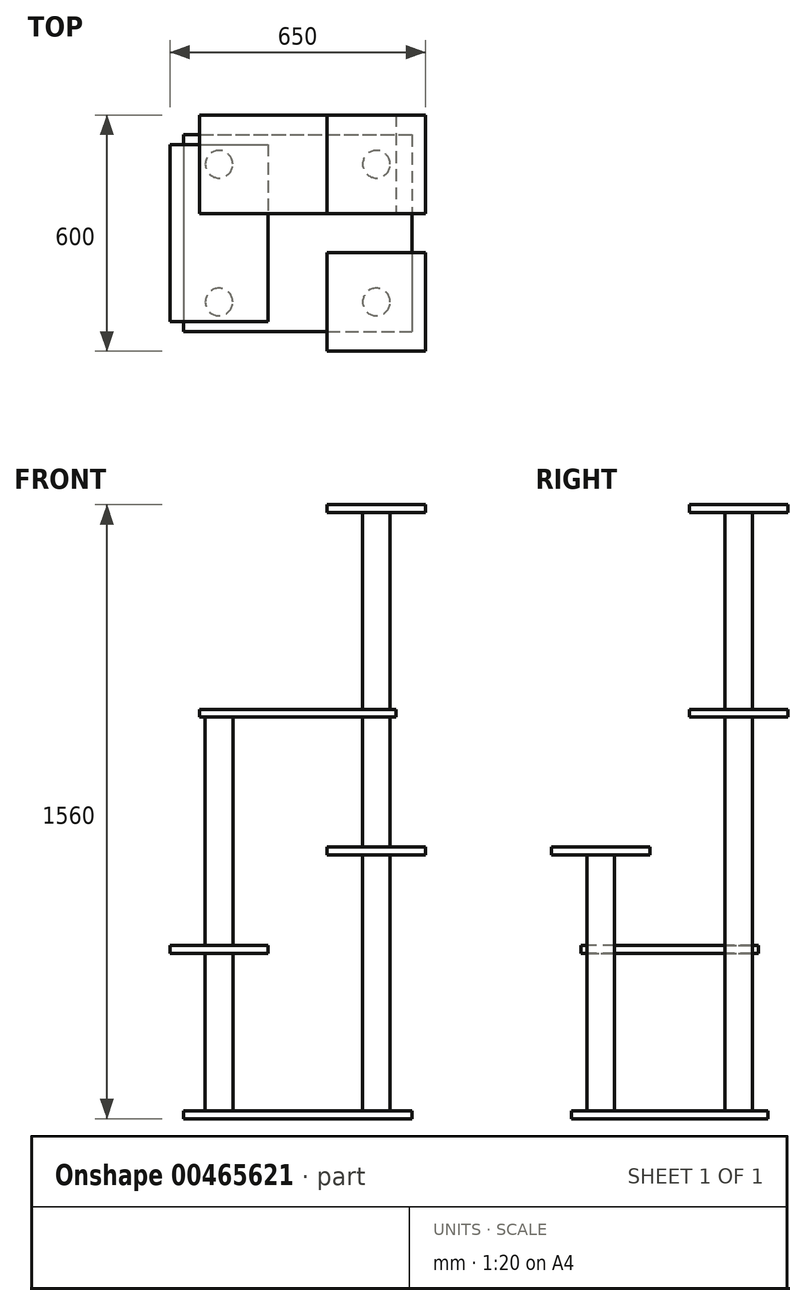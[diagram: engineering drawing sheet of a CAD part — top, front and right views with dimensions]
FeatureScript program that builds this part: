
annotation { "Feature Type Name" : "Feature", "Feature Type Description" : "" }
export const myFeature = defineFeature(function(context is Context, id is Id, definition is map)
    precondition{}
    {
        {
            var Q0;
            Q0=qCreatedBy(makeId("Top.planeOp"),FACE);
            var sketch = newSketch(context, id + "F0", { "sketchPlane" : qUnion([Q0])});
            skLineSegment(sketch, "E0.bottom", {"start": v(-290, 250) * mm, "end": v(290, 250) * mm});
            skLineSegment(sketch, "E0.top", {"start": v(-290, -250) * mm, "end": v(290, -250) * mm});
            skLineSegment(sketch, "E0.left", {"start": v(-290, 250) * mm, "end": v(-290, -250) * mm});
            skLineSegment(sketch, "E0.right", {"start": v(290, 250) * mm, "end": v(290, -250) * mm});
            skPoint(sketch, "E0.middle", {"position": v(0, 0) * mm});
            skSolve(sketch);
        }
        {
            var Q0;
            Q0=qSketchRegion(id+"F0",true);
            extrude(context, id + "F1", {"entities" : qUnion([Q0]), "depth" : 20 * mm});
        }
        {
            var Q0;
            Q0=makeQuery(id+"F1.opExtrude","CAP_FACE",FACE,{"disambiguationData":[OSD([sQuery(id+"F0.wireOp",EDGE,"E0.bottom"),sQuery(id+"F0.wireOp",EDGE,"E0.top"),sQuery(id+"F0.wireOp",EDGE,"E0.left"),sQuery(id+"F0.wireOp",EDGE,"E0.right")])],"isStart":false});
            var sketch = newSketch(context, id + "F2", { "sketchPlane" : qUnion([Q0])});
            skLineSegment(sketch, "E1.bottom", {"start": v(-200, 175) * mm, "end": v(200, 175) * mm, "construction": true});
            skLineSegment(sketch, "E1.top", {"start": v(-200, -175) * mm, "end": v(200, -175) * mm, "construction": true});
            skLineSegment(sketch, "E1.left", {"start": v(-200, 175) * mm, "end": v(-200, -175) * mm, "construction": true});
            skLineSegment(sketch, "E1.right", {"start": v(200, 175) * mm, "end": v(200, -175) * mm, "construction": true});
            skPoint(sketch, "E1.middle", {"position": v(0, 0) * mm});
            skCircle(sketch, "E2", {"center": v(-200, 175) * mm, "radius": 35 * mm});
            skCircle(sketch, "E3", {"center": v(200, 175) * mm, "radius": 35 * mm});
            skCircle(sketch, "E4", {"center": v(-200, -175) * mm, "radius": 35 * mm});
            skCircle(sketch, "E5", {"center": v(200, -175) * mm, "radius": 35 * mm});
            skSolve(sketch);
        }
        {
            var Q0;
            Q0=makeQuery(id+"F2.imprint","IMPRINT",FACE,{"disambiguationData":[TD([[makeQuery(id+"F2.imprint","IMPRINT",EDGE,{"derivedFrom":sQuery(id+"F2.wireOp",EDGE,"E2")}),1.0]])]});
            var Q1;
            Q1=makeQuery(id+"F2.imprint","IMPRINT",FACE,{"disambiguationData":[TD([[makeQuery(id+"F2.imprint","IMPRINT",EDGE,{"derivedFrom":sQuery(id+"F2.wireOp",EDGE,"E4")}),1.0]])]});
            extrude(context, id + "F3", {"entities" : qUnion([Q0, Q1]), "operationType" : NewBodyOperationType.ADD, "depth" : 400 * mm});
        }
        {
            var Q0;
            Q0=makeQuery(id+"F3.opExtrude","CAP_FACE",FACE,{"disambiguationData":[OSD([sQuery(id+"F2.wireOp",EDGE,"E2")])],"isStart":false});
            var sketch = newSketch(context, id + "F4", { "sketchPlane" : qUnion([Q0])});
            skLineSegment(sketch, "E6.bottom", {"start": v(-325, 225) * mm, "end": v(-75, 225) * mm});
            skLineSegment(sketch, "E6.top", {"start": v(-325, -225) * mm, "end": v(-75, -225) * mm});
            skLineSegment(sketch, "E6.left", {"start": v(-325, 225) * mm, "end": v(-325, -225) * mm});
            skLineSegment(sketch, "E6.right", {"start": v(-75, 225) * mm, "end": v(-75, -225) * mm});
            skPoint(sketch, "E6.middle", {"position": v(-200, 0) * mm});
            skLineSegment(sketch, "E7", {"start": v(-200, 175) * mm, "end": v(-200, -175) * mm, "construction": true});
            skSolve(sketch);
        }
        {
            var Q0;
            Q0=qSketchRegion(id+"F4",true);
            extrude(context, id + "F5", {"entities" : qUnion([Q0]), "operationType" : NewBodyOperationType.ADD, "depth" : 20 * mm});
        }
        {
            var Q0;
            Q0=makeQuery(id+"F2.imprint","IMPRINT",FACE,{"disambiguationData":[TD([[makeQuery(id+"F2.imprint","IMPRINT",EDGE,{"derivedFrom":sQuery(id+"F2.wireOp",EDGE,"E3")}),1.0]])]});
            extrude(context, id + "F6", {"entities" : qUnion([Q0]), "operationType" : NewBodyOperationType.ADD, "depth" : 1000 * mm});
        }
        {
            var Q0;
            Q0=makeQuery(id+"F5.opExtrude","CAP_FACE",FACE,{"disambiguationData":[OSD([sQuery(id+"F4.wireOp",EDGE,"E6.bottom"),sQuery(id+"F4.wireOp",EDGE,"E6.top"),sQuery(id+"F4.wireOp",EDGE,"E6.left"),sQuery(id+"F4.wireOp",EDGE,"E6.right")])],"isStart":false});
            var sketch = newSketch(context, id + "F7", { "sketchPlane" : qUnion([Q0])});
            skCircle(sketch, "E8.0", {"center": v(-200, 175) * mm, "radius": 35 * mm});
            skSolve(sketch);
        }
        {
            var Q0;
            Q0=makeQuery(id+"F7.imprint","IMPRINT",FACE,{"disambiguationData":[TD([[makeQuery(id+"F7.imprint","IMPRINT",EDGE,{"derivedFrom":sQuery(id+"F7.wireOp",EDGE,"E8.0")}),1.0]])]});
            var Q1;
            Q1=makeQuery(id+"F6.opExtrude","CAP_FACE",FACE,{"disambiguationData":[OSD([sQuery(id+"F2.wireOp",EDGE,"E3")])],"isStart":false});
            extrude(context, id + "F8", {"entities" : qUnion([Q0]), "operationType" : NewBodyOperationType.ADD, "endBound" : BoundingType.UP_TO_SURFACE, "endBoundEntityFace" : qUnion([Q1]), "depth" : 25 * mm});
        }
        {
            var Q0;
            Q0=makeQuery(id+"F2.imprint","IMPRINT",FACE,{"disambiguationData":[TD([[makeQuery(id+"F2.imprint","IMPRINT",EDGE,{"derivedFrom":sQuery(id+"F2.wireOp",EDGE,"E5")}),1.0]])]});
            extrude(context, id + "F9", {"entities" : qUnion([Q0]), "operationType" : NewBodyOperationType.ADD, "depth" : 650 * mm});
        }
        {
            var Q0;
            Q0=makeQuery(id+"F9.opExtrude","CAP_FACE",FACE,{"disambiguationData":[OSD([sQuery(id+"F2.wireOp",EDGE,"E5")])],"isStart":false});
            var sketch = newSketch(context, id + "F10", { "sketchPlane" : qUnion([Q0])});
            skLineSegment(sketch, "E9.bottom", {"start": v(75, -50) * mm, "end": v(325, -50) * mm});
            skLineSegment(sketch, "E9.top", {"start": v(75, -300) * mm, "end": v(325, -300) * mm});
            skLineSegment(sketch, "E9.left", {"start": v(75, -50) * mm, "end": v(75, -300) * mm});
            skLineSegment(sketch, "E9.right", {"start": v(325, -50) * mm, "end": v(325, -300) * mm});
            skPoint(sketch, "E9.middle", {"position": v(200, -175) * mm});
            skSolve(sketch);
        }
        {
            var Q0;
            Q0=makeQuery(id+"F10.imprint","IMPRINT",FACE,{"disambiguationData":[TD([[makeQuery(id+"F10.imprint","IMPRINT",EDGE,{"derivedFrom":sQuery(id+"F10.wireOp",EDGE,"E9.bottom")}),-1.0]])]});
            var Q1;
            Q1=makeQuery(id+"F10.imprint","IMPRINT",FACE,{"disambiguationData":[TD([[makeQuery(id+"F10.imprint","IMPRINT",EDGE,{"derivedFrom":makeQuery(id+"F9.opExtrude","CAP_EDGE",EDGE,{"disambiguationData":[OSD([sQuery(id+"F2.wireOp",EDGE,"E5")])],"isStart":false})}),1.0]])]});
            extrude(context, id + "F11", {"entities" : qUnion([Q0, Q1]), "operationType" : NewBodyOperationType.ADD, "depth" : 20 * mm});
        }
        {
            var Q0;
            Q0=makeQuery(id+"F8.opExtrude","CAP_FACE",FACE,{"disambiguationData":[OSD([sQuery(id+"F7.wireOp",EDGE,"E8.0")])],"isStart":false});
            var sketch = newSketch(context, id + "F12", { "sketchPlane" : qUnion([Q0])});
            skLineSegment(sketch, "E10.bottom", {"start": v(-250, 300) * mm, "end": v(250, 300) * mm});
            skLineSegment(sketch, "E10.top", {"start": v(-250, 50) * mm, "end": v(250, 50) * mm});
            skLineSegment(sketch, "E10.left", {"start": v(-250, 300) * mm, "end": v(-250, 50) * mm});
            skLineSegment(sketch, "E10.right", {"start": v(250, 300) * mm, "end": v(250, 50) * mm});
            skPoint(sketch, "E10.middle", {"position": v(0, 175) * mm});
            skLineSegment(sketch, "E11.0", {"start": v(-200, 175) * mm, "end": v(200, 175) * mm, "construction": true});
            skSolve(sketch);
        }
        {
            var Q0;
            Q0=qSketchRegion(id+"F12",true);
            extrude(context, id + "F13", {"entities" : qUnion([Q0]), "operationType" : NewBodyOperationType.ADD, "depth" : 20 * mm});
        }
        {
            var Q0;
            Q0=makeQuery(id+"F13.opExtrude","CAP_FACE",FACE,{"disambiguationData":[OSD([sQuery(id+"F12.wireOp",EDGE,"E10.bottom"),sQuery(id+"F12.wireOp",EDGE,"E10.top"),sQuery(id+"F12.wireOp",EDGE,"E10.left"),sQuery(id+"F12.wireOp",EDGE,"E10.right")])],"isStart":false});
            var sketch = newSketch(context, id + "F14", { "sketchPlane" : qUnion([Q0])});
            skCircle(sketch, "E12.0", {"center": v(200, 175) * mm, "radius": 35 * mm});
            skSolve(sketch);
        }
        {
            var Q0;
            Q0=qSketchRegion(id+"F14",true);
            extrude(context, id + "F15", {"entities" : qUnion([Q0]), "operationType" : NewBodyOperationType.ADD, "depth" : 500 * mm});
        }
        {
            var Q0;
            Q0=makeQuery(id+"F15.opExtrude","CAP_FACE",FACE,{"disambiguationData":[OSD([sQuery(id+"F14.wireOp",EDGE,"E12.0")])],"isStart":false});
            var sketch = newSketch(context, id + "F16", { "sketchPlane" : qUnion([Q0])});
            skLineSegment(sketch, "E13.bottom", {"start": v(75, 300) * mm, "end": v(325, 300) * mm});
            skLineSegment(sketch, "E13.top", {"start": v(75, 50) * mm, "end": v(325, 50) * mm});
            skLineSegment(sketch, "E13.left", {"start": v(75, 300) * mm, "end": v(75, 50) * mm});
            skLineSegment(sketch, "E13.right", {"start": v(325, 300) * mm, "end": v(325, 50) * mm});
            skPoint(sketch, "E13.middle", {"position": v(200, 175) * mm});
            skSolve(sketch);
        }
        {
            var Q0;
            Q0=qSketchRegion(id+"F16",true);
            extrude(context, id + "F17", {"entities" : qUnion([Q0]), "operationType" : NewBodyOperationType.ADD, "depth" : 20 * mm});
        }
    });
